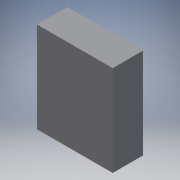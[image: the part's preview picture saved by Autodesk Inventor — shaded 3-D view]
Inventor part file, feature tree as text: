
AUTODESK INVENTOR PART (.ipt)
format: ipt  version: 2018.3 (Build 223284000, 284)  size: 80,384 bytes
history: native  units: mm
features: extrude x1, sketch x1
ambient origin geometry x8: Origin, YZ Plane, XZ Plane, XY Plane, X Axis, Y Axis, Z Axis, Center Point
bodies: Solid1 (feature_tree)
feature tree (2):
  extrude  "Extrusion1"  Depth=2.0mm
  sketch  "Sketch1"  dims[d0=5.0mm d1=2.0mm d2=6.0mm d3=0.0mm]
